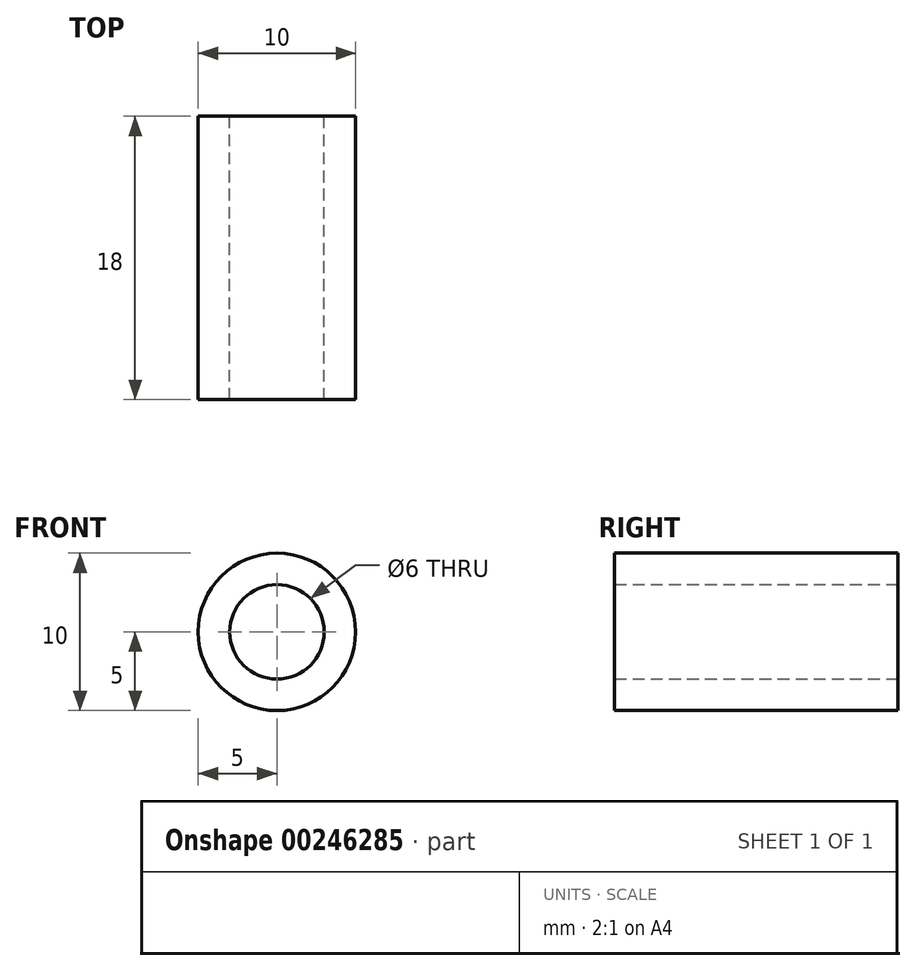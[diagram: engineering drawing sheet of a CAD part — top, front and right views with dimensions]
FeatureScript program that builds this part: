
annotation { "Feature Type Name" : "Feature", "Feature Type Description" : "" }
export const myFeature = defineFeature(function(context is Context, id is Id, definition is map)
    precondition{}
    {
        {
            var Q0;
            Q0=qCreatedBy(makeId("Front.planeOp"),FACE);
            var sketch = newSketch(context, id + "F0", { "sketchPlane" : qUnion([Q0])});
            skCircle(sketch, "E0", {"center": v(0, 0) * mm, "radius": 3 * mm});
            skCircle(sketch, "E1", {"center": v(0, 0) * mm, "radius": 5 * mm});
            skSolve(sketch);
        }
        {
            var Q0;
            Q0 = qSketchRegion(id + "F0", true);
            extrude(context, id + "F1", {"entities" : qUnion([Q0]), "depth" : 18 * mm});
        }
    });
